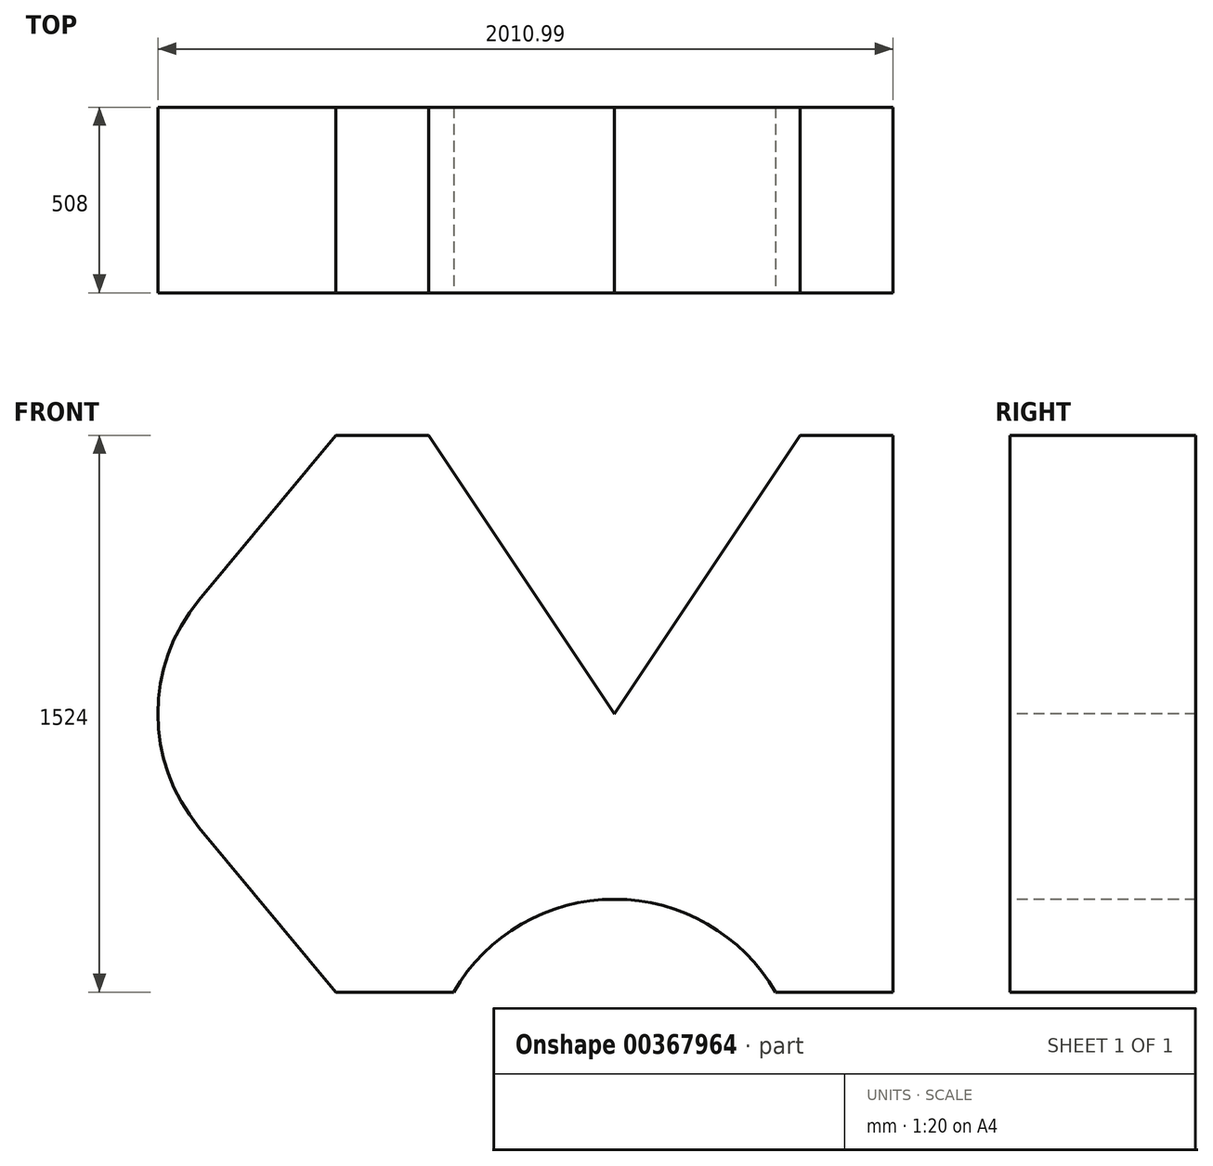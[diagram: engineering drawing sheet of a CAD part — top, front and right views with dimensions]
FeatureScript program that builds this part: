
annotation { "Feature Type Name" : "Feature", "Feature Type Description" : "" }
export const myFeature = defineFeature(function(context is Context, id is Id, definition is map)
    precondition{}
    {
        {
            var Q0;
            Q0=qCreatedBy(makeId("Front.planeOp"),FACE);
            var sketch = newSketch(context, id + "F0", { "sketchPlane" : qUnion([Q0])});
            skLineSegment(sketch, "E0", {"start": v(0, 0) * mm, "end": v(508, 762) * mm});
            skLineSegment(sketch, "E1", {"start": v(508, 762) * mm, "end": v(762, 762) * mm});
            skLineSegment(sketch, "E2", {"start": v(762, 762) * mm, "end": v(762, -762) * mm});
            skLineSegment(sketch, "E3", {"start": v(762, -762) * mm, "end": v(439.94, -762) * mm});
            skArc(sketch, "E4", {"start": v(439.94, -762) * mm, "mid": v(0, -508) * mm, "end": v(-439.94, -762) * mm});
            skLineSegment(sketch, "E5", {"start": v(-439.94, -762) * mm, "end": v(-762, -762) * mm});
            skLineSegment(sketch, "E6", {"start": v(-762, -762) * mm, "end": v(-1136.56, -311.23) * mm});
            skLineSegment(sketch, "E7", {"start": v(0, 0) * mm, "end": v(-508, 762) * mm});
            skLineSegment(sketch, "E8", {"start": v(-508, 762) * mm, "end": v(-762, 762) * mm});
            skLineSegment(sketch, "E9", {"start": v(-762, 762) * mm, "end": v(-1136.56, 311.23) * mm});
            skArc(sketch, "E10", {"start": v(-1136.56, 311.23) * mm, "mid": v(-1248.99, 0) * mm, "end": v(-1136.56, -311.23) * mm});
            skLineSegment(sketch, "E11", {"start": v(-762, 762) * mm, "end": v(-762, -762) * mm, "construction": true});
            skSolve(sketch);
        }
        {
            var Q0;
            Q0=makeQuery(id+"F0.imprint","IMPRINT",FACE,{"disambiguationData":[TD([[makeQuery(id+"F0.imprint","IMPRINT",EDGE,{"derivedFrom":sQuery(id+"F0.wireOp",EDGE,"E0")}),-1.0]])]});
            extrude(context, id + "F1", {"entities" : qUnion([Q0]), "oppositeDirection" : true, "depth" : 508 * mm});
        }
    });
